# Revit family: 0066609-PM
name_source: partatom
category: Lighting Fixtures
revit_build: Autodesk Revit 2017 (Build: 20190507_1515(x64)
units: mm (PartAtom-declared; Revit-internal decimal feet)

## family parameters
Cut with Voids When Loaded = No
Host = Face
Light Source = Yes
OmniClass Number = 23.80.70.00
OmniClass Title = Lighting
Part Type = Normal
Room Calculation Point = No
Round Connector Dimension = Use Diameter
Shared = No

## types (1)
- Type Name
    Apparent Load = 0 VA
    Assembly Code = 0066609 SKS S 1-5KLM NW XR18  I 9022
    AssetType = 0066609
    ClassificationValue = Fixed
    Color Filter = 16777215
    Cost = 0 $
    Default Elevation = 1219 mm
    Description = The Skyline Street family is dedicated for road lighting applications. Light distribution: XR18 - Extra Wide Road, color temperature: 4000K , total system power: 49W, total fixture output: 4902lm, luminaire efficacy: 100lm/W, LOR: 100%, colour rendering index: 70, LED Chromaticity: 5 step MacAdam ellipse tolerance, lifetime: 100000 hours at L90B50 @ 50°C, energy class: A++, A+, A, operating voltage: 220-240V / 50-60Hz, electronic driver, Without Controls, power factor: min. 0.9, electrical protection: Class I, Ingress protection rating: IP66, Impact resistance: IK08, dimensions: 525x255x105mm, weight: 6 kg, for 42-60mm side entry or post top installation with +/-15° adjustability, the housing is made of Die Cast Aluminium in RAL9022 color combined with tempered flat glass cover.
    Dimming Lamp Color Temperature Shift = <None>
    DocumentationLiterature = http://www.sylvania-lighting.com
    DurationUnit = Class I
    ElectricShockClassification = IK08
    Emit Shape Visible in Rendering = No
    Emit from Rectangle Length = 1219 mm
    Emit from Rectangle Width = 610 mm
    ExpectedLife = 16500
    Height = 0 mm  [stored 0 ft]
    IfcExportAs = 100 lm/W
    IfcExportType = Feilo Sylvania
    ImpactProtectionIndex = 255
    IngressProtection = 105
    InputNominalFrequency = 0066609.ies
    InputVoltage = 49 W
    Lamp = http://www.sylvania-lighting.com
    LampsType = http://www.sylvania-lighting.com
    Length = 525 mm
    LightOutputRatio = 0066609 Sylvania Lighting Fixture Skyline Street S 1-5klm NW XR18  I 9022: 0066609 SKS S 1-5KLM NW XR18  I 9022
    Manufacturer = Feilo Sylvania
    ManufacturerName = Feilo Sylvania
    Material_1_FEILO = <By Category>
    Material_2_FEILO = <By Category>
    Material_3_FEILO = <By Category>
    Material_4_FEILO = <By Category>
    NominalDepth = 0 mm  [stored 0 ft]
    NominalHeight = 0 mm  [stored 0 ft]
    NominalLength = 0 mm  [stored 0 ft]
    Photometric Web File = 0066609.ies
    PowerFactor = 0
    Tilt Angle = 60.00°
    Type Image = <None>
    URL = http://www.sylvania-lighting.com
    Voltage = 0 V
    Width = 255 mm  [stored 0.836614 ft]

note: [stored X ft] marks values corroborated as IEEE doubles in the binary element streams (Revit-internal decimal feet)

## geometry (parser evidence)
native form markers: Sweep x1
no freeform markers — native parametric forms only
